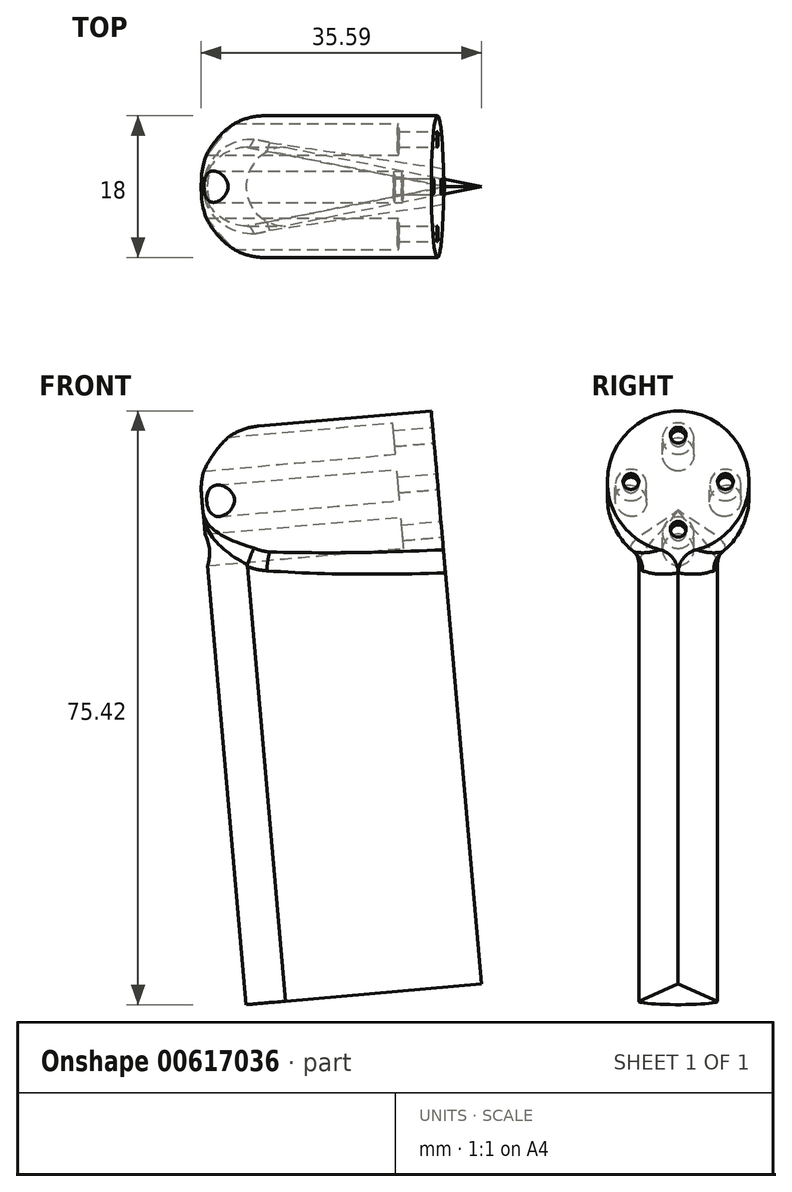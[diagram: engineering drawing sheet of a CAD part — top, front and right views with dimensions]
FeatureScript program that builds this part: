
annotation { "Feature Type Name" : "Feature", "Feature Type Description" : "" }
export const myFeature = defineFeature(function(context is Context, id is Id, definition is map)
    precondition{}
    {
        {
            var Q0;
            Q0=qCreatedBy(makeId("Top.planeOp"),FACE);
            var sketch = newSketch(context, id + "F0", { "sketchPlane" : qUnion([Q0])});
            skLineSegment(sketch, "E0.right", {"start": v(-15, 0) * mm, "end": v(-15, 0) * mm});
            skPoint(sketch, "E0.middle", {"position": v(0, 0) * mm});
            skPoint(sketch, "E1.visualSharp", {"position": v(-15, 5) * mm});
            skArc(sketch, "E1.filletArc", {"start": v(-10, 5) * mm, "mid": v(-13.54, 3.54) * mm, "end": v(-15, 0) * mm});
            skPoint(sketch, "E2.visualSharp", {"position": v(-15, -5) * mm});
            skArc(sketch, "E2.filletArc", {"start": v(-15, 0) * mm, "mid": v(-13.54, -3.54) * mm, "end": v(-10, -5) * mm});
            skLineSegment(sketch, "E3", {"start": v(-10, 5) * mm, "end": v(15, 0) * mm});
            skLineSegment(sketch, "E4", {"start": v(15, 0) * mm, "end": v(-10, -5) * mm});
            skPoint(sketch, "E5.orphan", {"position": v(15, -5) * mm});
            skPoint(sketch, "E0.left.end.orphan", {"position": v(15, 5) * mm});
            skSolve(sketch);
        }
        {
            var Q0;
            Q0=makeQuery(id+"F0.imprint","IMPRINT",FACE,{"disambiguationData":[TD([[makeQuery(id+"F0.imprint","IMPRINT",EDGE,{"derivedFrom":sQuery(id+"F0.wireOp",EDGE,"E1.filletArc")}),1.0]])]});
            extrude(context, id + "F1", {"entities" : qUnion([Q0]), "depth" : 64 * mm, "offsetDistance" : 25 * mm});
        }
        {
            var Q0;
            Q0=qCreatedBy(makeId("Front.planeOp"),FACE);
            var sketch = newSketch(context, id + "F2", { "sketchPlane" : qUnion([Q0])});
            skLineSegment(sketch, "E6", {"start": v(0, -6) * mm, "end": v(-15.02, -6) * mm});
            skLineSegment(sketch, "E7", {"start": v(-15.02, -9) * mm, "end": v(40, -9) * mm});
            skLineSegment(sketch, "E8", {"start": v(40, -9) * mm, "end": v(40, -6) * mm});
            skLineSegment(sketch, "E9", {"start": v(40, -6) * mm, "end": v(0, -6) * mm});
            skLineSegment(sketch, "E10", {"start": v(-15.02, 64.2) * mm, "end": v(-15.02, -29.08) * mm, "construction": true});
            skLineSegment(sketch, "E11", {"start": v(-15.02, -6) * mm, "end": v(-15.02, -9) * mm});
            skPoint(sketch, "E12.start.orphan", {"position": v(-40, -6) * mm});
            skSolve(sketch);
        }
        {
            var Q0;
            Q0=makeQuery(id+"F2.imprint","IMPRINT",FACE,{"disambiguationData":[TD([[makeQuery(id+"F2.imprint","IMPRINT",EDGE,{"derivedFrom":sQuery(id+"F2.wireOp",EDGE,"E6")}),1.0]])]});
            extrude(context, id + "F3", {"entities" : qUnion([Q0]), "operationType" : NewBodyOperationType.ADD, "endBound" : BoundingType.SYMMETRIC, "depth" : 25 * mm, "offsetDistance" : 25 * mm});
        }
        {
            var Q0;
            Q0=qCreatedBy(makeId("Right.planeOp"),FACE);
            cPlane(context, id + "F4", {"entities" : qUnion([Q0]), "cplaneType" : CPlaneType.OFFSET, "offset" : 15 * mm, "width" : 150 * mm, "height" : 150 * mm});
        }
        {
            var Q0;
            Q0=qCreatedBy(id+"F4.planeOp",FACE);
            var sketch = newSketch(context, id + "F5", { "sketchPlane" : qUnion([Q0])});
            skPoint(sketch, "E13", {"position": v(0, 64.08) * mm});
            skCircle(sketch, "E14", {"center": v(0, 64.08) * mm, "radius": 9 * mm});
            skSolve(sketch);
        }
        {
            var Q0;
            Q0 = qSketchRegion(id + "F5", true);
            extrude(context, id + "F6", {"entities" : qUnion([Q0]), "oppositeDirection" : true, "depth" : 30 * mm, "offsetDistance" : 25 * mm});
        }
        {
            var Q0;
            Q0=makeQuery(id+"F6.opExtrude","CAP_EDGE",EDGE,{"disambiguationData":[OSD([sQuery(id+"F5.wireOp",EDGE,"E14")])],"isStart":false});
            fillet(context, id + "F7", {"entities" : qUnion([Q0]), "radius" : 8 * mm, "tangentPropagation" : true, "allowEdgeOverflow" : false});
        }
        {
            var Q0;
            Q0=makeQuery(id+"F6.opExtrude","CAP_FACE",FACE,{"disambiguationData":[OSD([sQuery(id+"F5.wireOp",EDGE,"E14")])],"isStart":true});
            var sketch = newSketch(context, id + "F8", { "sketchPlane" : qUnion([Q0])});
            skCircle(sketch, "E15", {"center": v(0, 70) * mm, "radius": 2 * mm});
            skCircle(sketch, "E16", {"center": v(0, 58) * mm, "radius": 2 * mm});
            skLineSegment(sketch, "E17", {"start": v(0, 64.08) * mm, "end": v(-13.4, 64.08) * mm, "construction": true});
            skLineSegment(sketch, "E18", {"start": v(0, 64.08) * mm, "end": v(12, 64.08) * mm, "construction": true});
            skCircle(sketch, "E19", {"center": v(6, 64.08) * mm, "radius": 2 * mm});
            skCircle(sketch, "E20", {"center": v(-6, 64.08) * mm, "radius": 2 * mm});
            skSolve(sketch);
        }
        {
            var Q0;
            Q0=makeQuery(id+"F8.imprint","IMPRINT",FACE,{"disambiguationData":[TD([[makeQuery(id+"F8.imprint","IMPRINT",EDGE,{"derivedFrom":sQuery(id+"F8.wireOp",EDGE,"E15")}),1.0]])]});
            var Q1;
            Q1=makeQuery(id+"F8.imprint","IMPRINT",FACE,{"disambiguationData":[TD([[makeQuery(id+"F8.imprint","IMPRINT",EDGE,{"derivedFrom":sQuery(id+"F8.wireOp",EDGE,"E16")}),1.0]])]});
            var Q2;
            Q2=makeQuery(id+"F8.imprint","IMPRINT",FACE,{"disambiguationData":[TD([[makeQuery(id+"F8.imprint","IMPRINT",EDGE,{"derivedFrom":sQuery(id+"F8.wireOp",EDGE,"E20")}),1.0]])]});
            var Q3;
            Q3=makeQuery(id+"F8.imprint","IMPRINT",FACE,{"disambiguationData":[TD([[makeQuery(id+"F8.imprint","IMPRINT",EDGE,{"derivedFrom":sQuery(id+"F8.wireOp",EDGE,"E19")}),1.0]])]});
            extrude(context, id + "F9", {"entities" : qUnion([Q0, Q1, Q2, Q3]), "operationType" : NewBodyOperationType.REMOVE, "oppositeDirection" : true, "depth" : 50 * mm, "offsetDistance" : 25 * mm});
        }
        {
            var Q0;
            Q0=makeQuery(id+"F6.opExtrude","CAP_FACE",FACE,{"disambiguationData":[OSD([sQuery(id+"F5.wireOp",EDGE,"E14")])],"isStart":true});
            var sketch = newSketch(context, id + "F10", { "sketchPlane" : qUnion([Q0])});
            skCircle(sketch, "E21", {"center": v(0, 70) * mm, "radius": 1 * mm});
            skCircle(sketch, "E22", {"center": v(6, 64.08) * mm, "radius": 1 * mm});
            skCircle(sketch, "E23", {"center": v(0, 58) * mm, "radius": 1 * mm});
            skCircle(sketch, "E24", {"center": v(-6, 64.08) * mm, "radius": 1 * mm});
            skCircle(sketch, "E25", {"center": v(0, 58) * mm, "radius": 3 * mm});
            skCircle(sketch, "E26", {"center": v(6, 64.08) * mm, "radius": 3 * mm});
            skCircle(sketch, "E27", {"center": v(0, 70) * mm, "radius": 3 * mm});
            skCircle(sketch, "E28", {"center": v(-6, 64.08) * mm, "radius": 3 * mm});
            skSolve(sketch);
        }
        {
            var Q0;
            Q0=makeQuery(id+"F10.imprint","IMPRINT",FACE,{"disambiguationData":[TD([[makeQuery(id+"F10.imprint","IMPRINT",EDGE,{"derivedFrom":sQuery(id+"F10.wireOp",EDGE,"E28")}),1.0]])]});
            extrude(context, id + "F11", {"entities" : qUnion([Q0]), "operationType" : NewBodyOperationType.ADD, "oppositeDirection" : true, "depth" : 3 * mm, "offsetDistance" : 25 * mm});
        }
        {
            var Q0;
            Q0 = qSketchRegion(id + "F10", true);
            extrude(context, id + "F12", {"entities" : qUnion([Q0]), "oppositeDirection" : true, "depth" : 5 * mm, "offsetDistance" : 25 * mm});
        }
        {
            var Q0;
            Q0=makeQuery(id+"F12.opExtrude","SWEPT_BODY",BODY,{"disambiguationData":[OSD([sQuery(id+"F10.wireOp",EDGE,"E24"),sQuery(id+"F10.wireOp",EDGE,"E28")])]});
            var Q1;
            Q1=makeQuery(id+"F1.opExtrude","SWEPT_BODY",BODY,{"disambiguationData":[OSD([sQuery(id+"F0.wireOp",EDGE,"E1.filletArc"),sQuery(id+"F0.wireOp",EDGE,"E2.filletArc"),sQuery(id+"F0.wireOp",EDGE,"E3"),sQuery(id+"F0.wireOp",EDGE,"E4")])]});
            var Q2;
            Q2=makeQuery(id+"F6.opExtrude","SWEPT_BODY",BODY,{"disambiguationData":[OSD([sQuery(id+"F5.wireOp",EDGE,"E14")])]});
            var Q3;
            Q3=makeQuery(id+"F12.opExtrude","SWEPT_BODY",BODY,{"disambiguationData":[OSD([sQuery(id+"F10.wireOp",EDGE,"E21"),sQuery(id+"F10.wireOp",EDGE,"E27")])]});
            var Q4;
            Q4=makeQuery(id+"F12.opExtrude","SWEPT_BODY",BODY,{"disambiguationData":[OSD([sQuery(id+"F10.wireOp",EDGE,"E22"),sQuery(id+"F10.wireOp",EDGE,"E26")])]});
            var Q5;
            Q5=makeQuery(id+"F12.opExtrude","SWEPT_BODY",BODY,{"disambiguationData":[OSD([sQuery(id+"F10.wireOp",EDGE,"E23"),sQuery(id+"F10.wireOp",EDGE,"E25")])]});
            booleanBodies(context, id + "F13", {"operationType" : BooleanOperationType.UNION, "tools" : qUnion([Q0, Q1, Q2, Q3, Q4, Q5])});
        }
        {
            var Q0;
            Q0=makeQuery(id+"F13.opBoolean","INTERSECT",EDGE,{"derivedFrom":[makeQuery(id+"F6.opExtrude","SWEPT_FACE",FACE,{"disambiguationData":[OSD([sQuery(id+"F5.wireOp",EDGE,"E14")])]}),makeQuery(id+"F1.opExtrude","SWEPT_FACE",FACE,{"disambiguationData":[OSD([sQuery(id+"F0.wireOp",EDGE,"E4")])]})]});
            var Q1;
            Q1=makeQuery(id+"F13.opBoolean","INTERSECT",EDGE,{"derivedFrom":[makeQuery(id+"F1.opExtrude","SWEPT_FACE",FACE,{"disambiguationData":[OSD([sQuery(id+"F0.wireOp",EDGE,"E4")])]}),makeQuery(id+"F7.opFillet","BLEND_FACE",FACE,{"disambiguationData":[OSD([sQuery(id+"F5.wireOp",EDGE,"E14")])]})]});
            var Q2;
            Q2=makeQuery(id+"F13.opBoolean","INTERSECT",EDGE,{"derivedFrom":[makeQuery(id+"F1.opExtrude","SWEPT_FACE",FACE,{"disambiguationData":[OSD([sQuery(id+"F0.wireOp",EDGE,"E4")])]}),makeQuery(id+"F12.opExtrude","SWEPT_FACE",FACE,{"disambiguationData":[OSD([sQuery(id+"F10.wireOp",EDGE,"E25")])]})]});
            var Q3;
            Q3=makeQuery(id+"F13.opBoolean","INTERSECT",EDGE,{"disambiguationData":[OD(1.0)],"derivedFrom":[makeQuery(id+"F1.opExtrude","SWEPT_FACE",FACE,{"disambiguationData":[OSD([sQuery(id+"F0.wireOp",EDGE,"E1.filletArc"),sQuery(id+"F0.wireOp",EDGE,"E2.filletArc")])]}),makeQuery(id+"F7.opFillet","BLEND_FACE",FACE,{"disambiguationData":[OSD([sQuery(id+"F5.wireOp",EDGE,"E14")])]})]});
            var Q4;
            Q4=makeQuery(id+"F13.opBoolean","INTERSECT",EDGE,{"disambiguationData":[OD(0.0)],"derivedFrom":[makeQuery(id+"F1.opExtrude","SWEPT_FACE",FACE,{"disambiguationData":[OSD([sQuery(id+"F0.wireOp",EDGE,"E1.filletArc"),sQuery(id+"F0.wireOp",EDGE,"E2.filletArc")])]}),makeQuery(id+"F7.opFillet","BLEND_FACE",FACE,{"disambiguationData":[OSD([sQuery(id+"F5.wireOp",EDGE,"E14")])]})]});
            var Q5;
            Q5=makeQuery(id+"F13.opBoolean","INTERSECT",EDGE,{"derivedFrom":[makeQuery(id+"F1.opExtrude","SWEPT_FACE",FACE,{"disambiguationData":[OSD([sQuery(id+"F0.wireOp",EDGE,"E3")])]}),makeQuery(id+"F7.opFillet","BLEND_FACE",FACE,{"disambiguationData":[OSD([sQuery(id+"F5.wireOp",EDGE,"E14")])]})]});
            fillet(context, id + "F14", {"entities" : qUnion([Q0, Q1, Q2, Q3, Q4, Q5]), "radius" : 3 * mm, "tangentPropagation" : true, "allowEdgeOverflow" : false});
        }
        {
            var Q0;
            Q0 = qSketchRegion(id + "F0", true);
            extrude(context, id + "F15", {"entities" : qUnion([Q0]), "oppositeDirection" : true, "depth" : 8 * mm, "offsetDistance" : 25 * mm});
        }
        {
            var Q0;
            Q0=makeQuery(id+"F12.opExtrude","SWEPT_BODY",BODY,{"disambiguationData":[OSD([sQuery(id+"F10.wireOp",EDGE,"E24"),sQuery(id+"F10.wireOp",EDGE,"E28")])]});
            var Q1;
            Q1=makeQuery(id+"F3.opExtrude","SWEPT_EDGE",EDGE,{"disambiguationData":[OSD([sQuery(id+"F2.wireOp",EDGE,"E8"),sQuery(id+"F2.wireOp",EDGE,"E9")])]});
            transform(context, id + "F16", {"entities" : qUnion([Q0]), "transformType" : TransformType.ROTATION, "transformAxis" : qUnion([Q1]), "angle" : 5 * degree, "oppositeDirection" : true, "makeCopy" : false});
        }
        {
            var Q0;
            Q0=makeQuery(id+"F3.opExtrude","SWEPT_BODY",BODY,{"disambiguationData":[OSD([sQuery(id+"F2.wireOp",EDGE,"E6"),sQuery(id+"F2.wireOp",EDGE,"E7"),sQuery(id+"F2.wireOp",EDGE,"E8"),sQuery(id+"F2.wireOp",EDGE,"E9"),sQuery(id+"F2.wireOp",EDGE,"E11")])]});
            deleteBodies(context, id + "F17", {"entities" : qUnion([Q0])});
        }
        {
            var Q0;
            Q0=makeQuery(id+"F15.opExtrude","SWEPT_BODY",BODY,{"disambiguationData":[OSD([sQuery(id+"F0.wireOp",EDGE,"E1.filletArc"),sQuery(id+"F0.wireOp",EDGE,"E2.filletArc"),sQuery(id+"F0.wireOp",EDGE,"E3"),sQuery(id+"F0.wireOp",EDGE,"E4")])]});
            deleteBodies(context, id + "F18", {"entities" : qUnion([Q0])});
        }
    });
